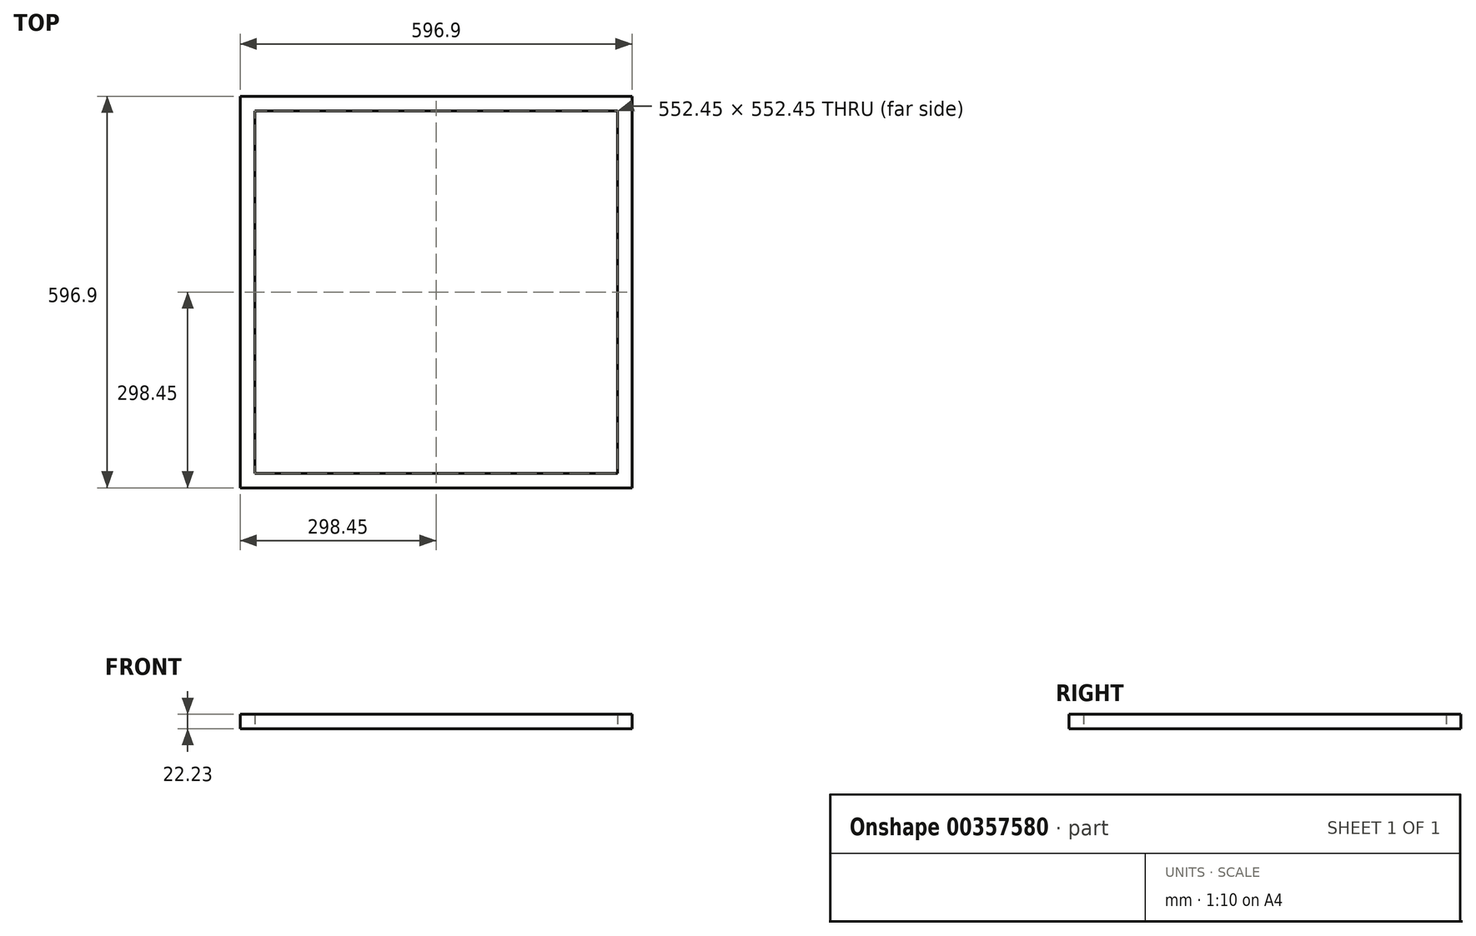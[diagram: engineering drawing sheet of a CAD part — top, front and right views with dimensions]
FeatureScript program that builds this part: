
annotation { "Feature Type Name" : "Feature", "Feature Type Description" : "" }
export const myFeature = defineFeature(function(context is Context, id is Id, definition is map)
    precondition{}
    {
        {
            var Q0;
            Q0=qCreatedBy(makeId("Top.planeOp"),FACE);
            var sketch = newSketch(context, id + "F0", { "sketchPlane" : qUnion([Q0])});
            skLineSegment(sketch, "E0.bottom", {"start": v(-298.45, 298.45) * mm, "end": v(298.45, 298.45) * mm});
            skLineSegment(sketch, "E0.top", {"start": v(-298.45, -298.45) * mm, "end": v(298.45, -298.45) * mm});
            skLineSegment(sketch, "E0.left", {"start": v(-298.45, 298.45) * mm, "end": v(-298.45, -298.45) * mm});
            skLineSegment(sketch, "E0.right", {"start": v(298.45, 298.45) * mm, "end": v(298.45, -298.45) * mm});
            skPoint(sketch, "E0.middle", {"position": v(0, 0) * mm});
            skLineSegment(sketch, "E1.0", {"start": v(-276.23, 276.22) * mm, "end": v(276.23, 276.23) * mm});
            skLineSegment(sketch, "E2.0", {"start": v(276.23, 276.23) * mm, "end": v(276.23, -276.23) * mm});
            skLineSegment(sketch, "E3.0", {"start": v(-276.23, -276.23) * mm, "end": v(276.23, -276.23) * mm});
            skLineSegment(sketch, "E4.0", {"start": v(-276.23, 276.22) * mm, "end": v(-276.23, -276.23) * mm});
            skSolve(sketch);
        }
        {
            var Q0;
            Q0=makeQuery(id+"F0.imprint","IMPRINT",FACE,{"disambiguationData":[TD([[makeQuery(id+"F0.imprint","IMPRINT",EDGE,{"derivedFrom":sQuery(id+"F0.wireOp",EDGE,"E0.bottom")}),-1.0]])]});
            extrude(context, id + "F1", {"entities" : qUnion([Q0]), "depth" : 22.22 * mm});
        }
        {
            var Q0;
            Q0=qCreatedBy(makeId("Top.planeOp"),FACE);
            var sketch = newSketch(context, id + "F2", { "sketchPlane" : qUnion([Q0])});
            skLineSegment(sketch, "E5.0", {"start": v(-276.23, 276.22) * mm, "end": v(276.23, 276.23) * mm});
            skLineSegment(sketch, "E6.0", {"start": v(-276.23, 276.22) * mm, "end": v(-276.23, -276.23) * mm});
            skLineSegment(sketch, "E7.0", {"start": v(276.23, 276.23) * mm, "end": v(276.23, -276.23) * mm});
            skLineSegment(sketch, "E8.0", {"start": v(-276.23, -276.23) * mm, "end": v(276.23, -276.23) * mm});
            skSolve(sketch);
        }
        {
            var Q0;
            Q0=makeQuery(id+"F2.imprint","IMPRINT",FACE,{"disambiguationData":[TD([[makeQuery(id+"F2.imprint","IMPRINT",EDGE,{"derivedFrom":sQuery(id+"F2.wireOp",EDGE,"E5.0")}),-1.0]])]});
            extrude(context, id + "F3", {"entities" : qUnion([Q0]), "depth" : 22.22 * mm});
        }
    });
